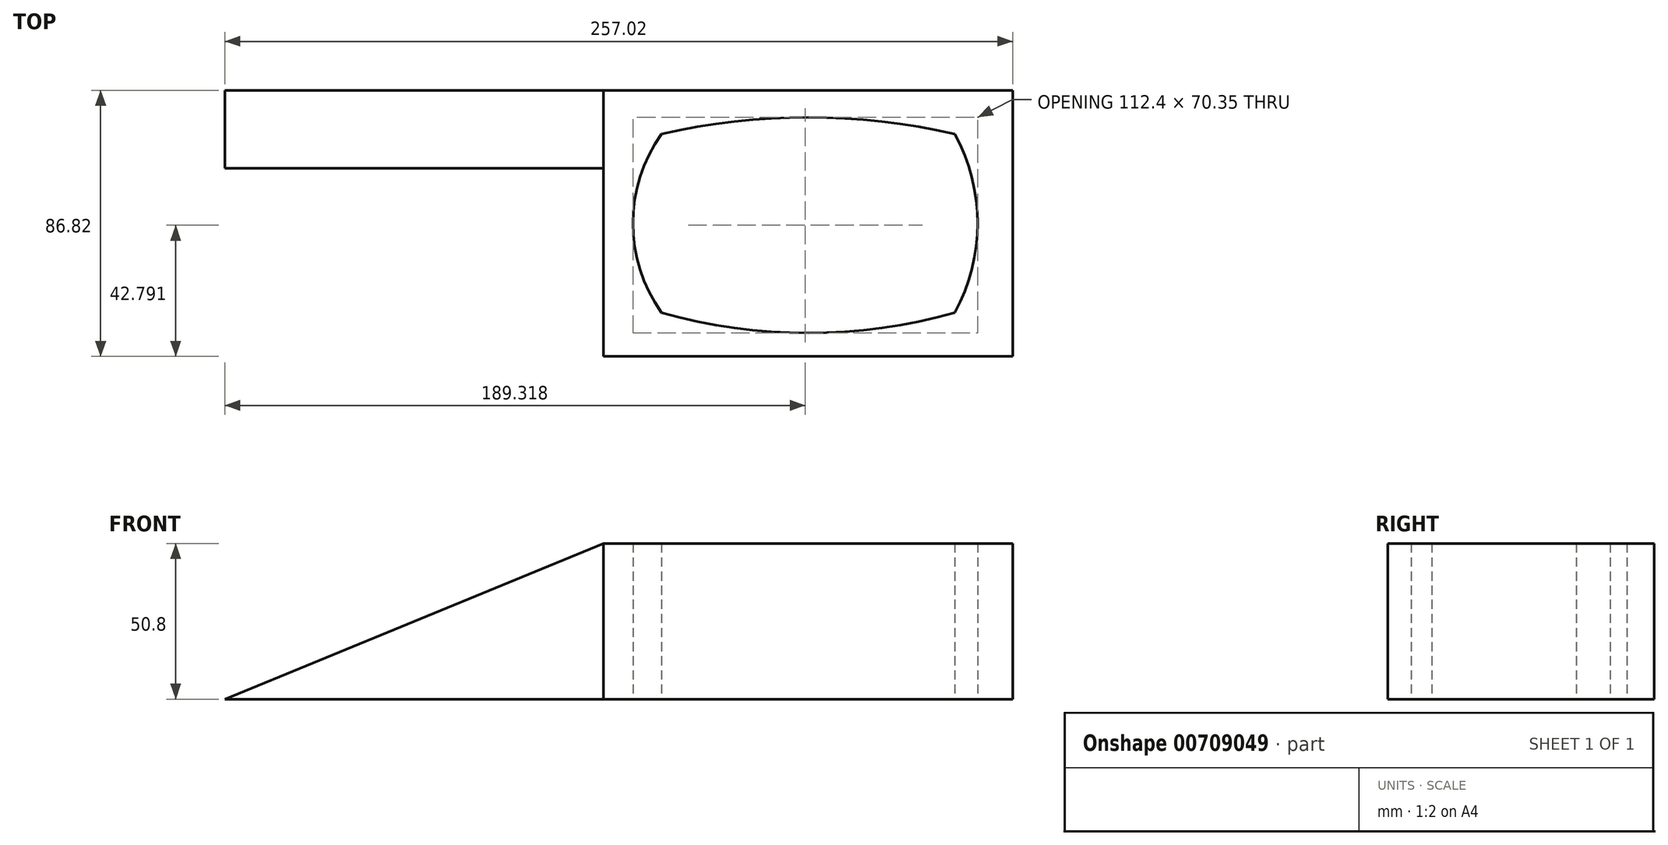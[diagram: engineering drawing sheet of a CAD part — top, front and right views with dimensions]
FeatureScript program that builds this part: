
annotation { "Feature Type Name" : "Feature", "Feature Type Description" : "" }
export const myFeature = defineFeature(function(context is Context, id is Id, definition is map)
    precondition{}
    {
        {
            var Q0;
            Q0=qCreatedBy(makeId("Top.planeOp"),FACE);
            var sketch = newSketch(context, id + "F0", { "sketchPlane" : qUnion([Q0])});
            skLineSegment(sketch, "E0.bottom", {"start": v(66.78, 43.4) * mm, "end": v(-66.78, 43.4) * mm});
            skLineSegment(sketch, "E0.top", {"start": v(66.78, -43.4) * mm, "end": v(-66.78, -43.4) * mm});
            skLineSegment(sketch, "E0.left", {"start": v(66.78, 43.4) * mm, "end": v(66.78, -43.4) * mm});
            skLineSegment(sketch, "E0.right", {"start": v(-66.78, 43.4) * mm, "end": v(-66.78, -43.4) * mm});
            skPoint(sketch, "E0.middle", {"position": v(0, 0) * mm});
            skLineSegment(sketch, "E1.bottom", {"start": v(47.8, 29.1) * mm, "end": v(-47.8, 29.1) * mm});
            skLineSegment(sketch, "E1.top", {"start": v(47.8, -29.1) * mm, "end": v(-47.8, -29.1) * mm});
            skLineSegment(sketch, "E1.left", {"start": v(47.8, 29.1) * mm, "end": v(47.8, -29.1) * mm});
            skLineSegment(sketch, "E1.right", {"start": v(-47.8, 29.1) * mm, "end": v(-47.8, -29.1) * mm});
            skArc(sketch, "E2", {"start": v(47.8, 29.1) * mm, "mid": v(0, 34.56) * mm, "end": v(-47.8, 29.1) * mm});
            skArc(sketch, "E3", {"start": v(-47.8, -29.1) * mm, "mid": v(0, -35.8) * mm, "end": v(47.8, -29.1) * mm});
            skArc(sketch, "E4", {"start": v(-47.8, 29.1) * mm, "mid": v(-57.12, 0) * mm, "end": v(-47.8, -29.1) * mm});
            skArc(sketch, "E5", {"start": v(47.8, -29.1) * mm, "mid": v(55.28, 0) * mm, "end": v(47.8, 29.1) * mm});
            skSolve(sketch);
        }
        {
            var Q0;
            Q0=makeQuery(id+"F0.imprint","IMPRINT",FACE,{"disambiguationData":[TD([[makeQuery(id+"F0.imprint","IMPRINT",EDGE,{"derivedFrom":sQuery(id+"F0.wireOp",EDGE,"E0.bottom")}),1.0]])]});
            var sketch = newSketch(context, id + "F1", { "sketchPlane" : qUnion([Q0])});
            skSolve(sketch);
        }
        {
            var Q0;
            Q0 = qSketchRegion(id + "F0", true);
            var Q1;
            Q1=makeQuery(id+"F1.imprint","IMPRINT",FACE,{"disambiguationData":[TD([[makeQuery(id+"F1.imprint","IMPRINT",EDGE,{"derivedFrom":makeQuery(id+"F0.imprint","IMPRINT",EDGE,{"derivedFrom":sQuery(id+"F0.wireOp",EDGE,"E2")})}),1.0]])]});
            extrude(context, id + "F2", {"entities" : qUnion([Q0, Q1]), "depth" : 50.8 * mm, "offsetDistance" : 25.4 * mm});
        }
        {
            var Q0;
            Q0=makeQuery(id+"F2.opExtrude","SWEPT_FACE",FACE,{"disambiguationData":[OSD([sQuery(id+"F0.wireOp",EDGE,"E0.bottom")])]});
            var sketch = newSketch(context, id + "F3", { "sketchPlane" : qUnion([Q0])});
            skLineSegment(sketch, "E6", {"start": v(66.78, 0) * mm, "end": v(190.24, 0) * mm});
            skLineSegment(sketch, "E7", {"start": v(190.24, 0) * mm, "end": v(66.78, 50.8) * mm});
            skLineSegment(sketch, "E8", {"start": v(66.78, 50.8) * mm, "end": v(66.78, 0) * mm});
            skSolve(sketch);
        }
        {
            var Q0;
            Q0 = qSketchRegion(id + "F3", true);
            extrude(context, id + "F4", {"entities" : qUnion([Q0]), "operationType" : NewBodyOperationType.ADD, "oppositeDirection" : true, "depth" : 25.4 * mm, "offsetDistance" : 25.4 * mm});
        }
    });
